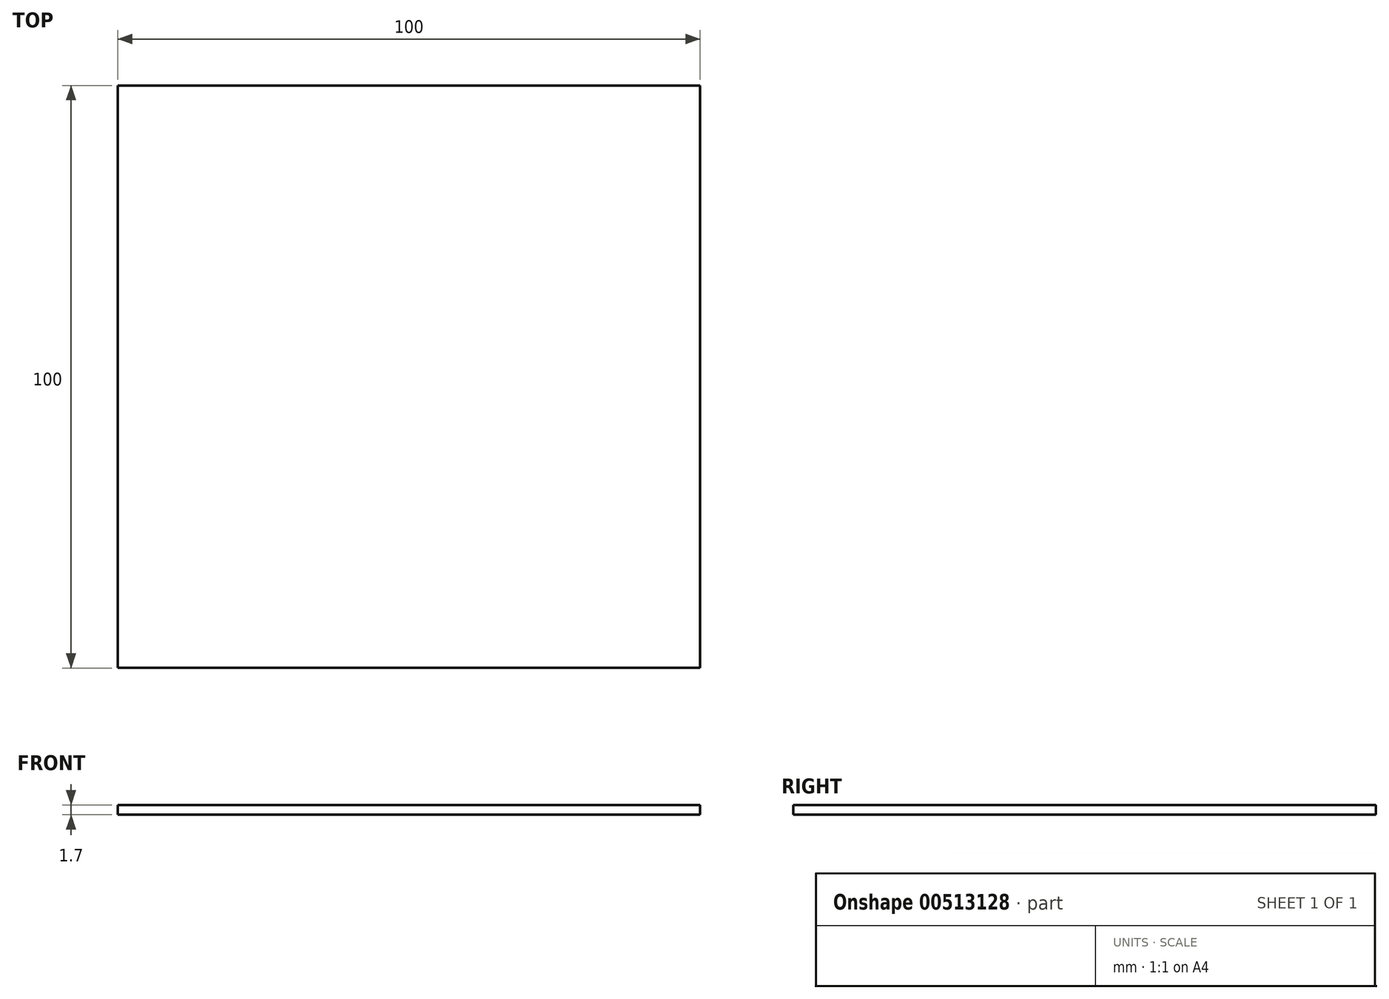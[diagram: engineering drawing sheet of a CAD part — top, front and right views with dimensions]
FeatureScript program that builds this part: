
annotation { "Feature Type Name" : "Feature", "Feature Type Description" : "" }
export const myFeature = defineFeature(function(context is Context, id is Id, definition is map)
    precondition{}
    {
        {
            var Q0;
            Q0=qCreatedBy(makeId("Top.planeOp"),FACE);
            var sketch = newSketch(context, id + "F0", { "sketchPlane" : qUnion([Q0])});
            skLineSegment(sketch, "E0.bottom", {"start": v(-86.65, 75.44) * mm, "end": v(13.35, 75.44) * mm});
            skLineSegment(sketch, "E0.top", {"start": v(-86.65, -24.56) * mm, "end": v(13.35, -24.56) * mm});
            skLineSegment(sketch, "E0.left", {"start": v(-86.65, 75.44) * mm, "end": v(-86.65, -24.56) * mm});
            skLineSegment(sketch, "E0.right", {"start": v(13.35, 75.44) * mm, "end": v(13.35, -24.56) * mm});
            skSolve(sketch);
        }
        {
            var Q0;
            Q0=makeQuery(id+"F0.imprint","IMPRINT",FACE,{"disambiguationData":[TD([[makeQuery(id+"F0.imprint","IMPRINT",EDGE,{"derivedFrom":sQuery(id+"F0.wireOp",EDGE,"E0.bottom")}),-1.0]])]});
            extrude(context, id + "F1", {"entities" : qUnion([Q0]), "depth" : 1.7 * mm});
        }
    });
